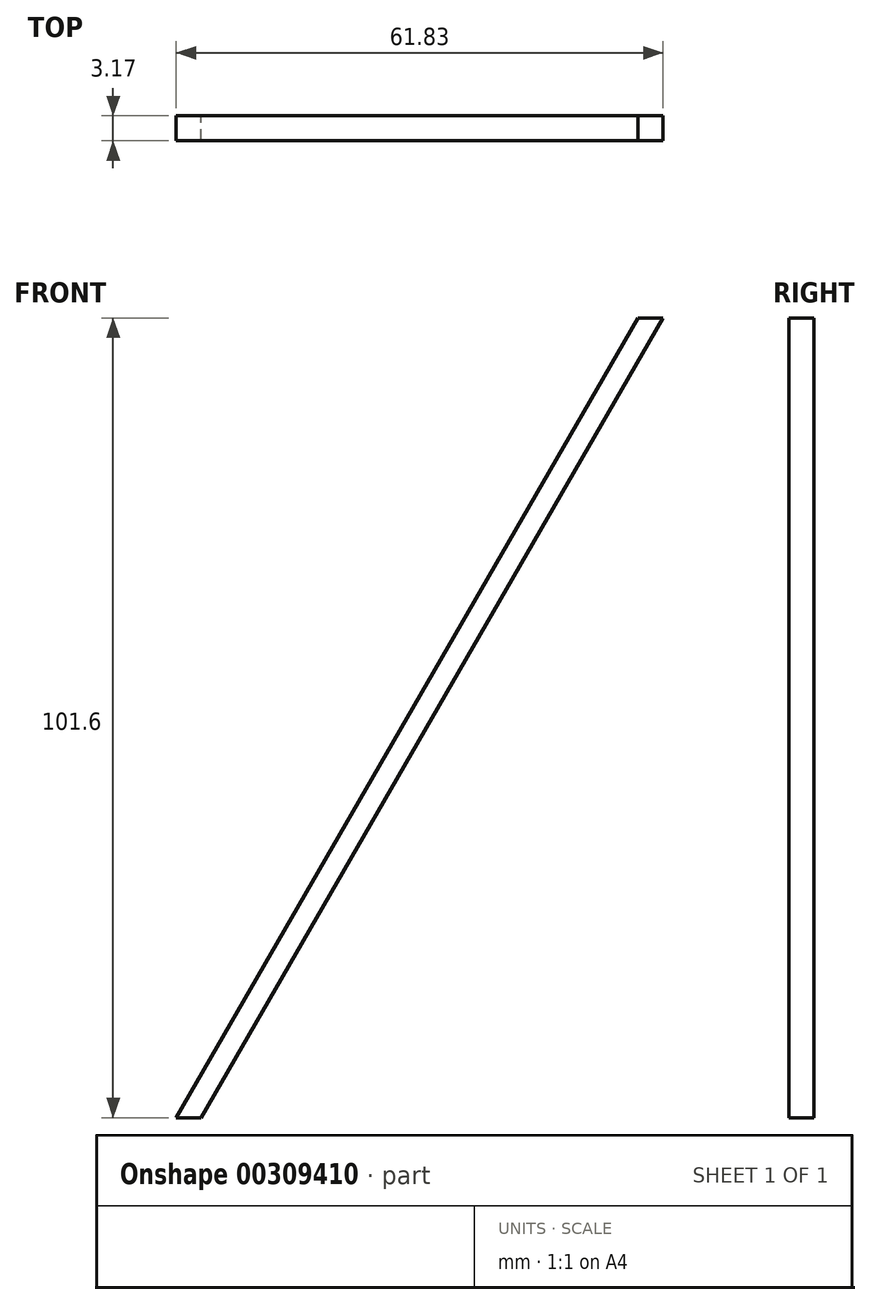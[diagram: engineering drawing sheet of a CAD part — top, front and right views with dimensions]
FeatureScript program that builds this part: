
annotation { "Feature Type Name" : "Feature", "Feature Type Description" : "" }
export const myFeature = defineFeature(function(context is Context, id is Id, definition is map)
    precondition{}
    {
        {
            var Q0;
            Q0=qCreatedBy(makeId("Front.planeOp"),FACE);
            var sketch = newSketch(context, id + "F0", { "sketchPlane" : qUnion([Q0])});
            skLineSegment(sketch, "E0", {"start": v(0, 0) * mm, "end": v(3.18, 0) * mm});
            skLineSegment(sketch, "E1", {"start": v(0, 0) * mm, "end": v(0, 0) * mm});
            skLineSegment(sketch, "E2", {"start": v(0, 0) * mm, "end": v(58.66, 101.6) * mm});
            skLineSegment(sketch, "E3", {"start": v(58.66, 101.6) * mm, "end": v(61.83, 101.6) * mm});
            skLineSegment(sketch, "E4", {"start": v(61.83, 101.6) * mm, "end": v(3.17, 0) * mm});
            skSolve(sketch);
        }
        {
            var Q0;
            Q0 = qSketchRegion(id + "F0", true);
            extrude(context, id + "F1", {"entities" : qUnion([Q0]), "depth" : 3.17 * mm});
        }
    });
